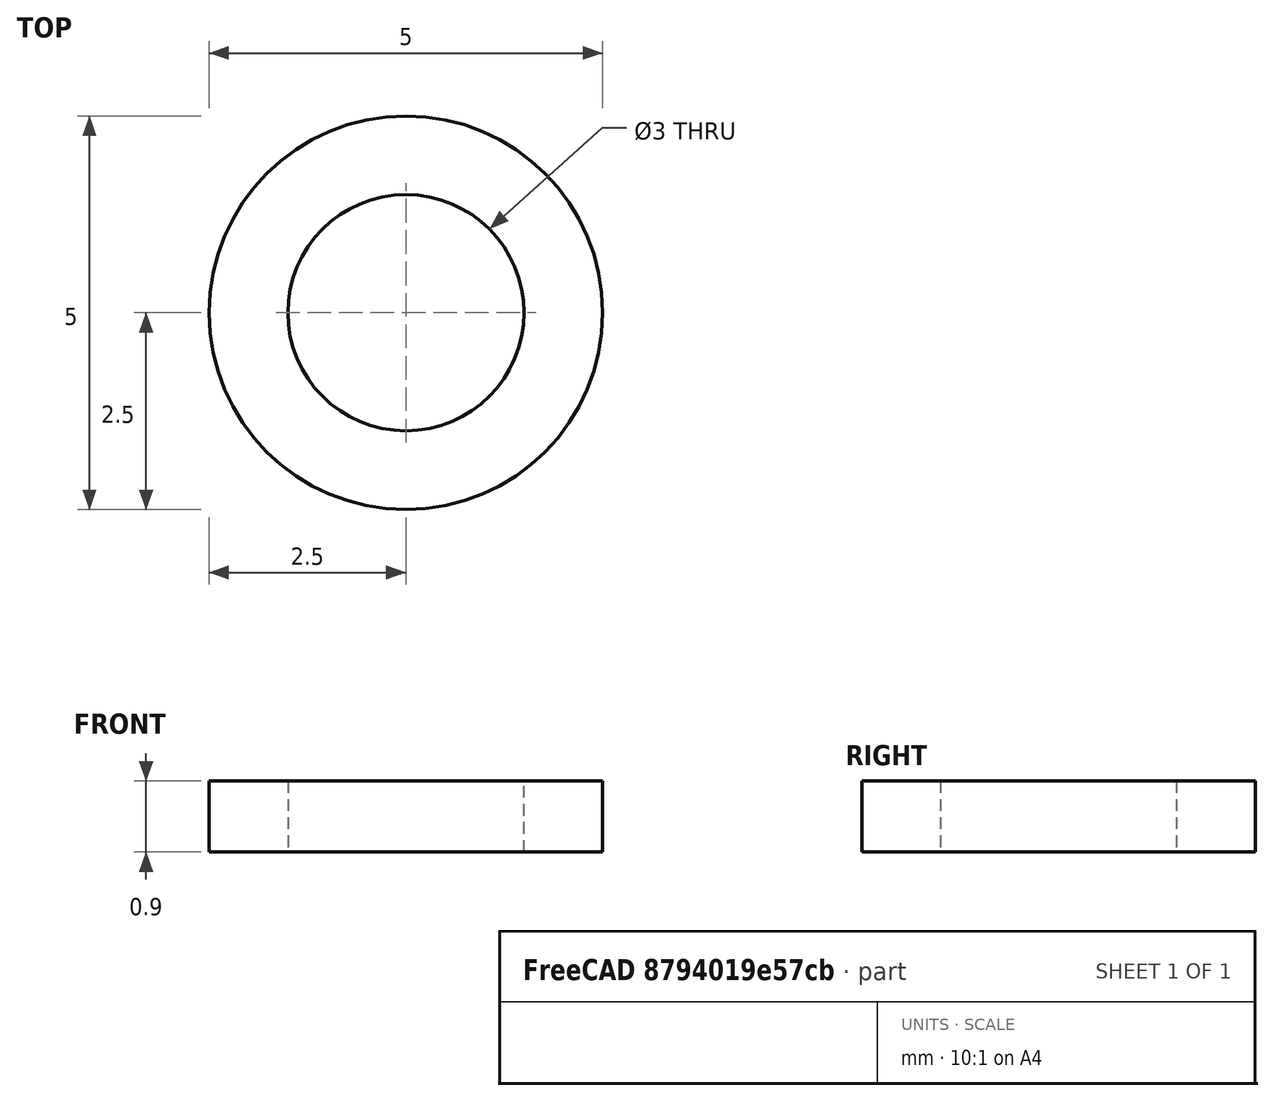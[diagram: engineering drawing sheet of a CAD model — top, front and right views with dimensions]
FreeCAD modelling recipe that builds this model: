
FCSTD DOCUMENT  (FreeCAD 1.0R39109 (Git))
Label: LED Holder 3mm
License: All rights reserved
LicenseURL: https://en.wikipedia.org/wiki/All_rights_reserved
objects: Sketcher::SketchObject×1, PartDesign::Pad×1, PartDesign::Body×1
note: 6 computed .brp shape members not serialized (recipe doc carries the construction recipe); baked Part::Feature solids carry a one-line shape summary decoded from their .brp

FEATURE [Sketcher::SketchObject] Sketch
  ArcFitTolerance = 1e-06
  AttachmentSupport = -> [XY_Plane]
  FullyConstrained = true
  MakeInternals = false
  MapMode = 5
  sketch-geometry (2):
    g0: Circle CenterX=0 CenterY=0 CenterZ=0 NormalX=0 NormalY=0 NormalZ=1 AngleXU=0 Radius=1.5
    g1: Circle CenterX=0 CenterY=0 CenterZ=0 NormalX=0 NormalY=0 NormalZ=1 AngleXU=0 Radius=2.5
  constraints (4):
    c: Coincident(g0,g-1)
    c: Coincident(g1,g0)
    c: Diameter(g0) = 3
    c: Diameter(g1) = 5
FEATURE [PartDesign::Pad] Pad
  Direction = (0,0,1)
  Length = 0.9
  Length2 = 10
  Profile = -> Sketch
  ReferenceAxis = -> Sketch [N_Axis]
  Refine = true
  Suppressed = false
  Type = 0
FEATURE [PartDesign::Body] Body
  AllowCompound = false
  Group = -> [Sketch,Pad]
  Origin = -> Origin
  Tip = -> Pad
